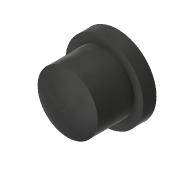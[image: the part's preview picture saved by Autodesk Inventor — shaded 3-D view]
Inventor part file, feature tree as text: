
AUTODESK INVENTOR PART (.ipt)
format: ipt  version: 2017 (Build 210142000, 142)  size: 105,984 bytes
history: native  units: in
note: dims shown in document units (in); Inventor stores cm internally (conversion verified against a paired STEP export)
features: other x4, reference x3, revolve x1, sketch x1
ambient origin geometry x8: Origin, YZ Plane, XZ Plane, XY Plane, X Axis, Y Axis, Z Axis, Center Point
bodies: Solid1 (feature_tree)
feature tree (9):
  revolve  "Revolution1"  Angle=90.0deg
  sketch  "Sketch1"  dims[d0=0.135in d1=90.0deg d2=0.25in d3=0.06in]
  reference  "Reference1"
  reference  "Reference2"
  reference  "Reference3"
  parser-record x1  (decoder bookkeeping rows leaked as tree rows — omitted from the tree; the rows remain in map.json)
  other  "Assembly1.iam"
  other  "Faceplate:1"
  other  "Button:1"
note: 1 file-system path scrubbed to <path> (originals preserved in map.json)
